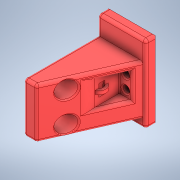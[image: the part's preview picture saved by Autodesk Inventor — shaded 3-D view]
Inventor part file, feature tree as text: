
AUTODESK INVENTOR PART (.ipt)
format: ipt  version: 2021 (Build 250183000, 183)  size: 757,248 bytes
history: native  units: mm
features: extrude x8, fillet x8, sketch x8, projected_geometry x8, delete_face x7, chamfer x6, other x4, reference x3, plane x2
ambient origin geometry x8: Origin, YZ Plane, XZ Plane, XY Plane, X Axis, Y Axis, Z Axis, Center Point
bodies: Volumenkörper1 (feature_tree), Body21 (feature_tree)
feature tree (54):
  extrude  "Extrusion1"  Depth=9.199998mm
  fillet  "Rundung1"  Radius=17.599996mm
  extrude  "Extrusion2"  Depth=1.0mm
  extrude  "Extrusion3"  Depth=5.8mm
  plane  "Arbeitsebene1"
  extrude  "Extrusion4"  TaperAngle=0.0deg  [1 undecoded]
  delete_face  "Fläche löschen1"
  delete_face  "Fläche löschen2"
  delete_face  "Fläche löschen3"
  delete_face  "Fläche löschen4"
  delete_face  "Fläche löschen5"
  extrude  "Extrusion5"  Depth=17.599996mm
  fillet  "Rundung2"  Radius=2.192622mm
  extrude  "Extrusion6"  Depth=2.192622mm
  chamfer  "Fase1"  Distance=12.0mm
  fillet  "Rundung3"  Radius=12.0mm
  chamfer  "Fase2"  Distance=1.0mm
  chamfer  "Fase3"  [1 undecoded]
  chamfer  "Fase4"  Distance=0.4mm Angle=45.0deg
  fillet  "Rundung4"  Radius=1.0mm
  fillet  "Rundung5"  Radius=0.4mm
  chamfer  "Fase5"  Distance=0.4mm Angle=45.0deg
  fillet  "Rundung6"  Radius=0.4mm
  plane  "Arbeitsebene2"
  extrude  "Extrusion7"  Depth=1.0mm
  extrude  "Extrusion8"  Depth=10.0mm
  chamfer  "Fase6"  Distance=0.4mm Angle=45.0deg
  fillet  "Rundung7"  Radius=1.0mm
  fillet  "Rundung8"  Radius=5.0mm
  delete_face  "Fläche löschen6"
  delete_face  "Fläche löschen7"
  sketch  "Skizze1"  dims[d0=18.399996mm d1=9.199998mm d2=17.599996mm]
  reference  "Referenz1"
  reference  "Referenz2"
  reference  "Referenz3"
  projected_geometry  "Projizierte Kontur1"
  sketch  "Skizze2"  dims[d3=15.0mm d4=0.0mm d5=1.0mm]
  projected_geometry  "Projizierte Kontur2"
  projected_geometry  "Projizierte Kontur3"
  sketch  "Skizze3"  dims[d6=5.8mm d7=5.8mm]
  projected_geometry  "Projizierte Kontur4"
  sketch  "Skizze4"  dims[d8=12.0mm d9=0.0mm d10=0.0mm d11=0.0mm]
  sketch  "Skizze5"  dims[d12=8.5mm d13=17.599996mm d15=2.192622mm]
  projected_geometry  "Projizierte Kontur5"
  sketch  "Skizze6"  dims[d16=2.385243mm d17=2.192622mm]
  sketch  "Skizze7"  dims[d18=2.192622mm]
  projected_geometry  "Projizierte Kontur6"
  projected_geometry  "Projizierte Kontur7"
  projected_geometry  "Projizierte Kontur8"
  sketch  "Skizze8"  dims[d19=2.192622mm d20=12.0mm d21=0.0mm d22=12.0mm d23=0.0mm d24=1.0mm d25=0.0mm d26=0.0mm d27=0.4mm d28=2.0mm d29=45.0deg d30=1.0mm d31=0.4mm d32=2.0mm d33=45.0deg d34=0.4mm d35=2.0mm d36=45.0deg d37=0.4mm d38=2.0mm d39=45.0deg d40=1.0mm d41=10.0mm d42=0.4mm d43=2.0mm d44=45.0deg d45=1.0mm d46=5.0mm d47=3.0mm d48=1.0mm d49=1.2mm d50=0.0mm d51=2.0mm d52=3.0mm d53=1.0mm d54=0.0mm d55=0.6mm d56=2.0mm d57=45.0deg d58=5.0mm d59=4.0mm]
  other  "<userpath>\Downloads\VORON2_v2.4_Assembly.step\X Carriage.iam"
  other  "X Carriage.iam"
  other  "X Carriage Frame:1"
  other  "Bauteil264"
note: 2 required parameter values undecoded (feature->parameter linkage not recoverable at this tier; creation-order binding heuristic only, values carry confidence <= 0.55)
